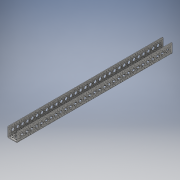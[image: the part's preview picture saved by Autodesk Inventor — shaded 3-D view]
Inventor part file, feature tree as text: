
AUTODESK INVENTOR PART (.ipt)
format: ipt  version: 2016 (Build 200138000, 138)  size: 1,735,680 bytes
history: native  units: in
note: dims shown in document units (in); Inventor stores cm internally (conversion verified against a paired STEP export)
features: fillet x1
ambient origin geometry x8: Origin, YZ Plane, XZ Plane, XY Plane, X Axis, Y Axis, Z Axis, Center Point
bodies: Solid1 (feature_tree)
feature tree (1):
  fillet  "Fillet1"  [1 undecoded]
note: 1 required parameter value undecoded (feature->parameter linkage not recoverable at this tier; creation-order binding heuristic only, values carry confidence <= 0.55)
